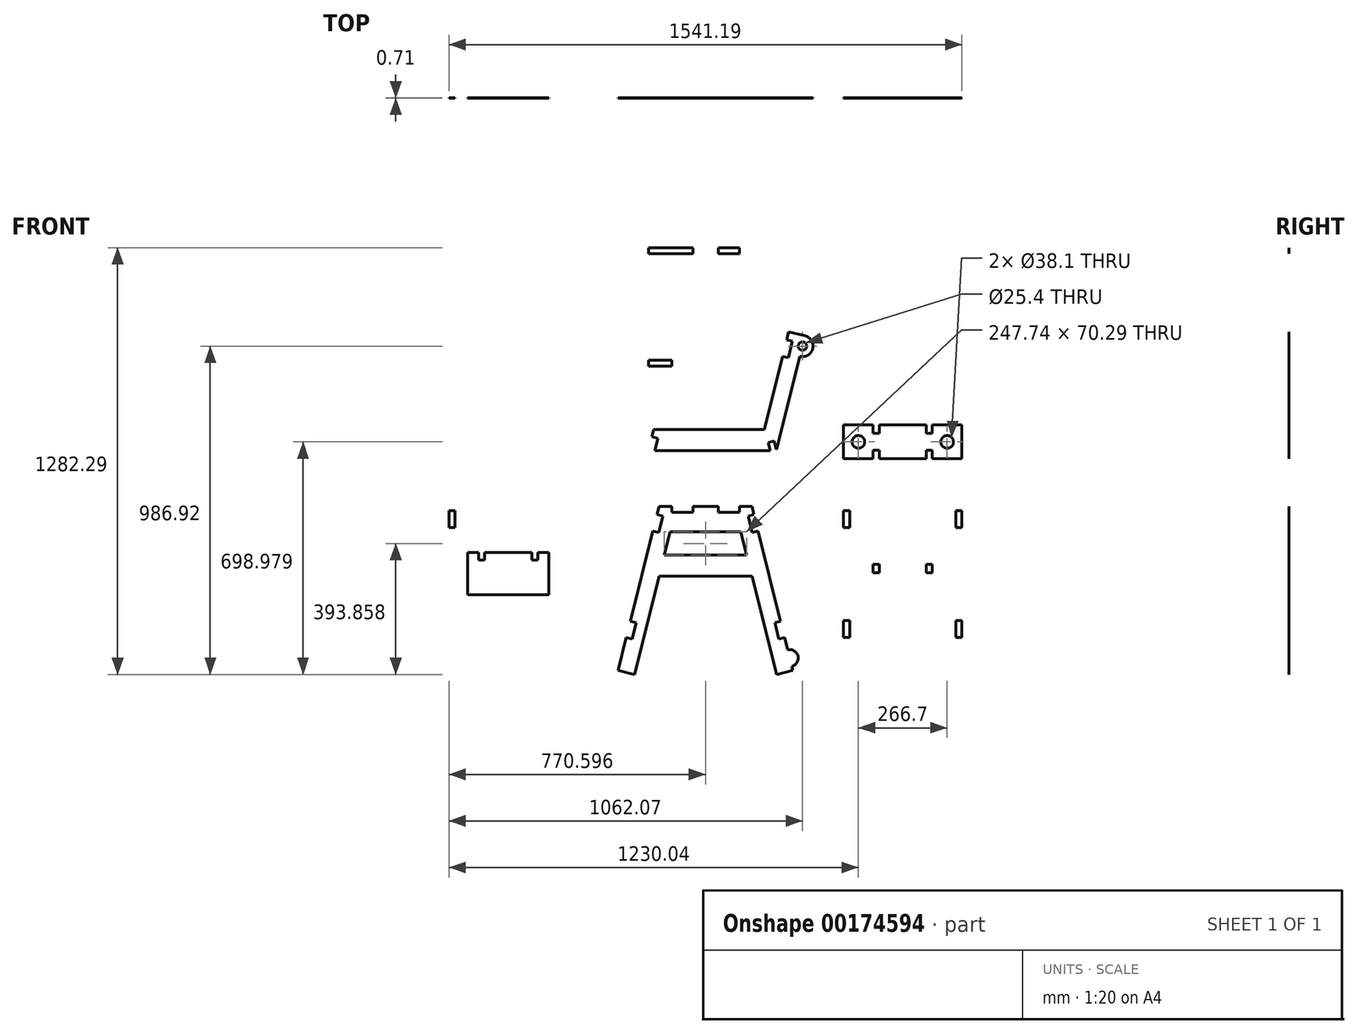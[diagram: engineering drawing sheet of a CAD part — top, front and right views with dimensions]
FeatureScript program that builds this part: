
annotation { "Feature Type Name" : "Feature", "Feature Type Description" : "" }
export const myFeature = defineFeature(function(context is Context, id is Id, definition is map)
    precondition{}
    {
        {
            assignVariable(context, id + "F0", {"name" : "MaterialThickness", "anyValue" : .71});
        }
        {
            var Q0;
            Q0=qCreatedBy(makeId("Front.planeOp"),FACE);
            var sketch = newSketch(context, id + "F1", { "sketchPlane" : qUnion([Q0])});
            skLineSegment(sketch, "E0", {"start": v(0, 0) * mm, "end": v(525.2, 0) * mm, "construction": true});
            skLineSegment(sketch, "E1", {"start": v(0, 0) * mm, "end": v(122.9, 492.91) * mm});
            skLineSegment(sketch, "E2", {"start": v(0, 0) * mm, "end": v(0, 165.04) * mm, "construction": true});
            skLineSegment(sketch, "E3", {"start": v(122.9, 492.91) * mm, "end": v(172.19, 480.62) * mm});
            skLineSegment(sketch, "E4", {"start": v(172.19, 480.62) * mm, "end": v(49.3, -12.29) * mm});
            skLineSegment(sketch, "E5", {"start": v(49.3, -12.29) * mm, "end": v(0, 0) * mm});
            skLineSegment(sketch, "E6.bottom", {"start": v(122.9, 492.91) * mm, "end": v(402.3, 492.91) * mm});
            skLineSegment(sketch, "E6.top", {"start": v(122.9, 416.71) * mm, "end": v(402.3, 416.71) * mm});
            skLineSegment(sketch, "E6.left", {"start": v(122.9, 492.91) * mm, "end": v(122.9, 416.71) * mm});
            skLineSegment(sketch, "E6.right", {"start": v(402.3, 492.91) * mm, "end": v(402.3, 416.71) * mm});
            skLineSegment(sketch, "E7", {"start": v(122.9, 282.93) * mm, "end": v(402.3, 282.93) * mm});
            skLineSegment(sketch, "E8.0", {"start": v(122.9, 346.43) * mm, "end": v(402.3, 346.43) * mm});
            skLineSegment(sketch, "E9", {"start": v(122.9, 346.43) * mm, "end": v(122.9, 282.93) * mm});
            skLineSegment(sketch, "E10", {"start": v(402.3, 282.93) * mm, "end": v(402.3, 346.43) * mm});
            skLineSegment(sketch, "E11", {"start": v(262.6, 416.71) * mm, "end": v(262.6, 0) * mm, "construction": true});
            skLineSegment(sketch, "E12.0", {"start": v(116.75, 468.26) * mm, "end": v(166.04, 455.98) * mm, "construction": true});
            skLineSegment(sketch, "E13.bottom", {"start": v(116.75, 468.26) * mm, "end": v(134.25, 463.9) * mm});
            skLineSegment(sketch, "E13.top", {"start": v(104.46, 418.97) * mm, "end": v(121.96, 414.61) * mm});
            skLineSegment(sketch, "E13.left", {"start": v(116.75, 468.26) * mm, "end": v(104.46, 418.97) * mm});
            skLineSegment(sketch, "E13.right", {"start": v(134.25, 463.9) * mm, "end": v(121.96, 414.61) * mm});
            skLineSegment(sketch, "E14.0", {"start": v(24.58, 98.58) * mm, "end": v(73.87, 86.3) * mm, "construction": true});
            skLineSegment(sketch, "E15.bottom", {"start": v(36.87, 147.87) * mm, "end": v(54.37, 143.51) * mm});
            skLineSegment(sketch, "E15.top", {"start": v(24.58, 98.58) * mm, "end": v(42.08, 94.22) * mm});
            skLineSegment(sketch, "E15.left", {"start": v(36.87, 147.87) * mm, "end": v(24.58, 98.58) * mm});
            skLineSegment(sketch, "E15.right", {"start": v(54.37, 143.51) * mm, "end": v(42.08, 94.22) * mm});
            skLineSegment(sketch, "E16.bottom", {"start": v(161, 492.91) * mm, "end": v(224.5, 492.91) * mm});
            skLineSegment(sketch, "E16.top", {"start": v(161, 474.88) * mm, "end": v(224.5, 474.88) * mm});
            skLineSegment(sketch, "E16.left", {"start": v(161, 492.91) * mm, "end": v(161, 474.88) * mm});
            skLineSegment(sketch, "E16.right", {"start": v(224.5, 492.91) * mm, "end": v(224.5, 474.88) * mm});
            skLineSegment(sketch, "E17", {"start": v(262.6, 492.91) * mm, "end": v(262.6, 416.71) * mm, "construction": true});
            skLineSegment(sketch, "E18.0", {"start": v(224.5, 492.91) * mm, "end": v(224.5, 416.71) * mm, "construction": true});
            skLineSegment(sketch, "E19.MirrorCS", {"start": v(525.2, 0) * mm, "end": v(402.3, 492.91) * mm});
            skLineSegment(sketch, "E20.MirrorCS", {"start": v(408.44, 468.26) * mm, "end": v(359.15, 455.98) * mm, "construction": true});
            skLineSegment(sketch, "E21.MirrorCS", {"start": v(500.61, 98.58) * mm, "end": v(451.32, 86.3) * mm, "construction": true});
            skLineSegment(sketch, "E22.MirrorCS", {"start": v(525.2, 0) * mm, "end": v(525.2, 165.04) * mm, "construction": true});
            skLineSegment(sketch, "E23.MirrorCS", {"start": v(353, 480.62) * mm, "end": v(475.9, -12.29) * mm});
            skLineSegment(sketch, "E24.MirrorCS", {"start": v(475.9, -12.29) * mm, "end": v(525.2, 0) * mm});
            skLineSegment(sketch, "E25.MirrorCS", {"start": v(402.3, 492.91) * mm, "end": v(353, 480.62) * mm});
            skLineSegment(sketch, "E26.MirrorCS", {"start": v(500.61, 98.58) * mm, "end": v(483.12, 94.22) * mm});
            skLineSegment(sketch, "E27.MirrorCS", {"start": v(420.73, 418.97) * mm, "end": v(403.23, 414.61) * mm});
            skLineSegment(sketch, "E28.MirrorCS", {"start": v(390.94, 463.9) * mm, "end": v(403.23, 414.61) * mm});
            skLineSegment(sketch, "E29.MirrorCS", {"start": v(488.32, 147.87) * mm, "end": v(500.61, 98.58) * mm});
            skLineSegment(sketch, "E30.MirrorCS", {"start": v(408.44, 468.26) * mm, "end": v(390.94, 463.9) * mm});
            skLineSegment(sketch, "E31.MirrorCS", {"start": v(488.32, 147.87) * mm, "end": v(470.83, 143.51) * mm});
            skLineSegment(sketch, "E32.MirrorCS", {"start": v(470.83, 143.51) * mm, "end": v(483.12, 94.22) * mm});
            skLineSegment(sketch, "E33.MirrorCS", {"start": v(408.44, 468.26) * mm, "end": v(420.73, 418.97) * mm});
            skLineSegment(sketch, "E34.MirrorCS", {"start": v(364.2, 492.91) * mm, "end": v(300.7, 492.91) * mm});
            skLineSegment(sketch, "E35.MirrorCS", {"start": v(364.2, 492.91) * mm, "end": v(364.2, 474.88) * mm});
            skLineSegment(sketch, "E36.MirrorCS", {"start": v(364.2, 474.88) * mm, "end": v(300.7, 474.88) * mm});
            skLineSegment(sketch, "E37.MirrorCS", {"start": v(300.7, 492.91) * mm, "end": v(300.7, 474.88) * mm});
            skLineSegment(sketch, "E38.bottom", {"start": v(-152.4, 98.58) * mm, "end": v(-508, 98.58) * mm});
            skLineSegment(sketch, "E38.top", {"start": v(-152.4, 479.58) * mm, "end": v(-508, 479.58) * mm});
            skLineSegment(sketch, "E38.left", {"start": v(-152.4, 98.58) * mm, "end": v(-152.4, 479.58) * mm});
            skLineSegment(sketch, "E38.right", {"start": v(-508, 98.58) * mm, "end": v(-508, 479.58) * mm});
            skLineSegment(sketch, "E39.bottom", {"start": v(-152.4, 479.58) * mm, "end": v(-170.43, 479.58) * mm});
            skLineSegment(sketch, "E39.top", {"start": v(-152.4, 428.78) * mm, "end": v(-170.43, 428.78) * mm});
            skLineSegment(sketch, "E39.left", {"start": v(-152.4, 479.58) * mm, "end": v(-152.4, 428.78) * mm});
            skLineSegment(sketch, "E39.right", {"start": v(-170.43, 479.58) * mm, "end": v(-170.43, 428.78) * mm});
            skLineSegment(sketch, "E40.bottom", {"start": v(-152.4, 98.58) * mm, "end": v(-170.43, 98.58) * mm});
            skLineSegment(sketch, "E40.top", {"start": v(-152.4, 149.38) * mm, "end": v(-170.43, 149.38) * mm});
            skLineSegment(sketch, "E40.left", {"start": v(-152.4, 98.58) * mm, "end": v(-152.4, 149.38) * mm});
            skLineSegment(sketch, "E40.right", {"start": v(-170.43, 98.58) * mm, "end": v(-170.43, 149.38) * mm});
            skLineSegment(sketch, "E41.bottom", {"start": v(-170.43, 479.58) * mm, "end": v(-208.53, 479.58) * mm});
            skLineSegment(sketch, "E41.top", {"start": v(-170.43, 98.58) * mm, "end": v(-208.53, 98.58) * mm});
            skLineSegment(sketch, "E41.left", {"start": v(-170.43, 479.58) * mm, "end": v(-170.43, 98.58) * mm});
            skLineSegment(sketch, "E41.right", {"start": v(-208.53, 479.58) * mm, "end": v(-208.53, 98.58) * mm});
            skLineSegment(sketch, "E42", {"start": v(-330.2, 479.58) * mm, "end": v(-330.2, 98.58) * mm, "construction": true});
            skLineSegment(sketch, "E43.bottom", {"start": v(-208.53, 354.01) * mm, "end": v(-330.2, 354.01) * mm});
            skLineSegment(sketch, "E43.top", {"start": v(-208.53, 227.01) * mm, "end": v(-330.2, 227.01) * mm});
            skLineSegment(sketch, "E43.left", {"start": v(-208.53, 354.01) * mm, "end": v(-208.53, 227.01) * mm});
            skLineSegment(sketch, "E43.right", {"start": v(-330.2, 354.01) * mm, "end": v(-330.2, 227.01) * mm});
            skLineSegment(sketch, "E44", {"start": v(122.9, 346.43) * mm, "end": v(86.37, 346.43) * mm, "construction": true});
            skLineSegment(sketch, "E45", {"start": v(116.75, 468.26) * mm, "end": v(86.37, 346.43) * mm, "construction": true});
            skLineSegment(sketch, "E46", {"start": v(-279.4, 354.01) * mm, "end": v(-279.4, 479.58) * mm, "construction": true});
            skLineSegment(sketch, "E47.MirrorCS", {"start": v(-489.97, 98.58) * mm, "end": v(-489.97, 149.38) * mm});
            skLineSegment(sketch, "E48.MirrorCS", {"start": v(-451.87, 354.01) * mm, "end": v(-451.87, 227.01) * mm});
            skLineSegment(sketch, "E49.MirrorCS", {"start": v(-508, 98.58) * mm, "end": v(-489.97, 98.58) * mm});
            skLineSegment(sketch, "E50.MirrorCS", {"start": v(-489.97, 479.58) * mm, "end": v(-489.97, 428.78) * mm});
            skLineSegment(sketch, "E51.MirrorCS", {"start": v(-508, 149.38) * mm, "end": v(-489.97, 149.38) * mm});
            skLineSegment(sketch, "E52.MirrorCS", {"start": v(-451.87, 354.01) * mm, "end": v(-330.2, 354.01) * mm});
            skLineSegment(sketch, "E53.MirrorCS", {"start": v(-451.87, 227.01) * mm, "end": v(-330.2, 227.01) * mm});
            skLineSegment(sketch, "E54.MirrorCS", {"start": v(-508, 428.78) * mm, "end": v(-489.97, 428.78) * mm});
            skLineSegment(sketch, "E55.MirrorCS", {"start": v(-508, 98.58) * mm, "end": v(-508, 149.38) * mm});
            skLineSegment(sketch, "E56.MirrorCS", {"start": v(-489.97, 479.58) * mm, "end": v(-451.87, 479.58) * mm});
            skLineSegment(sketch, "E57.MirrorCS", {"start": v(-489.97, 479.58) * mm, "end": v(-489.97, 98.58) * mm});
            skLineSegment(sketch, "E58.MirrorCS", {"start": v(-489.97, 98.58) * mm, "end": v(-451.87, 98.58) * mm});
            skLineSegment(sketch, "E59.MirrorCS", {"start": v(-508, 479.58) * mm, "end": v(-489.97, 479.58) * mm});
            skLineSegment(sketch, "E60.MirrorCS", {"start": v(-451.87, 479.58) * mm, "end": v(-451.87, 98.58) * mm});
            skLineSegment(sketch, "E61.MirrorCS", {"start": v(-508, 479.58) * mm, "end": v(-508, 428.78) * mm});
            skLineSegment(sketch, "E62", {"start": v(121.96, 414.61) * mm, "end": v(54.37, 143.51) * mm, "construction": true});
            skLineSegment(sketch, "E63.bottom", {"start": v(405.36, 295.21) * mm, "end": v(454.65, 282.93) * mm, "construction": true});
            skLineSegment(sketch, "E63.top", {"start": v(491.39, 640.25) * mm, "end": v(540.68, 627.96) * mm, "construction": true});
            skLineSegment(sketch, "E63.left", {"start": v(405.36, 295.21) * mm, "end": v(491.39, 640.25) * mm, "construction": true});
            skLineSegment(sketch, "E63.right", {"start": v(454.65, 282.93) * mm, "end": v(540.68, 627.96) * mm, "construction": true});
            skLineSegment(sketch, "E64", {"start": v(402.3, 282.93) * mm, "end": v(454.65, 282.93) * mm, "construction": true});
            skLineSegment(sketch, "E65", {"start": v(470.83, 143.51) * mm, "end": v(403.23, 414.61) * mm, "construction": true});
            skLineSegment(sketch, "E66", {"start": v(436.07, 282.93) * mm, "end": v(453.56, 287.29) * mm, "construction": true});
            skLineSegment(sketch, "E67", {"start": v(453.56, 287.29) * mm, "end": v(473.5, 292.26) * mm, "construction": true});
            skLineSegment(sketch, "E68.0", {"start": v(429.92, 307.57) * mm, "end": v(447.42, 311.93) * mm, "construction": true});
            skLineSegment(sketch, "E69", {"start": v(402.3, 346.43) * mm, "end": v(418.13, 346.43) * mm, "construction": true});
            skLineSegment(sketch, "E70", {"start": v(427.76, 390.8) * mm, "end": v(410.26, 386.44) * mm});
            skLineSegment(sketch, "E71", {"start": v(122.9, 282.93) * mm, "end": v(70.54, 282.93) * mm, "construction": true});
            skLineSegment(sketch, "E72", {"start": v(89.13, 282.93) * mm, "end": v(71.63, 287.29) * mm, "construction": true});
            skLineSegment(sketch, "E73.bottom", {"start": v(71.63, 287.29) * mm, "end": v(89.13, 282.93) * mm, "construction": true});
            skLineSegment(sketch, "E73.top", {"start": v(80.85, 324.26) * mm, "end": v(98.34, 319.9) * mm, "construction": true});
            skLineSegment(sketch, "E73.left", {"start": v(71.63, 287.29) * mm, "end": v(80.85, 324.26) * mm, "construction": true});
            skLineSegment(sketch, "E73.right", {"start": v(89.13, 282.93) * mm, "end": v(98.34, 319.9) * mm, "construction": true});
            skLineSegment(sketch, "E74.bottom", {"start": v(677.6, 98.58) * mm, "end": v(1033.2, 98.58) * mm});
            skLineSegment(sketch, "E74.top", {"start": v(677.6, 479.58) * mm, "end": v(1033.2, 479.58) * mm});
            skLineSegment(sketch, "E74.left", {"start": v(677.6, 98.58) * mm, "end": v(677.6, 479.58) * mm});
            skLineSegment(sketch, "E74.right", {"start": v(1033.2, 98.58) * mm, "end": v(1033.2, 479.58) * mm});
            skLineSegment(sketch, "E75", {"start": v(855.4, 479.58) * mm, "end": v(855.4, 98.58) * mm, "construction": true});
            skLineSegment(sketch, "E76.bottom", {"start": v(677.6, 479.58) * mm, "end": v(695.63, 479.58) * mm});
            skLineSegment(sketch, "E76.top", {"start": v(677.6, 428.78) * mm, "end": v(695.63, 428.78) * mm});
            skLineSegment(sketch, "E76.left", {"start": v(677.6, 479.58) * mm, "end": v(677.6, 428.78) * mm});
            skLineSegment(sketch, "E76.right", {"start": v(695.63, 479.58) * mm, "end": v(695.63, 428.78) * mm});
            skLineSegment(sketch, "E77.bottom", {"start": v(695.63, 149.38) * mm, "end": v(677.6, 149.38) * mm});
            skLineSegment(sketch, "E77.top", {"start": v(695.63, 98.58) * mm, "end": v(677.6, 98.58) * mm});
            skLineSegment(sketch, "E77.left", {"start": v(695.63, 149.38) * mm, "end": v(695.63, 98.58) * mm});
            skLineSegment(sketch, "E77.right", {"start": v(677.6, 149.38) * mm, "end": v(677.6, 98.58) * mm});
            skLineSegment(sketch, "E78.bottom", {"start": v(695.63, 479.58) * mm, "end": v(733.73, 479.58) * mm});
            skLineSegment(sketch, "E78.top", {"start": v(695.63, 98.58) * mm, "end": v(733.73, 98.58) * mm});
            skLineSegment(sketch, "E78.left", {"start": v(695.63, 479.58) * mm, "end": v(695.63, 98.58) * mm});
            skLineSegment(sketch, "E78.right", {"start": v(733.73, 479.58) * mm, "end": v(733.73, 98.58) * mm});
            skPoint(sketch, "E79", {"position": v(419, 388.62) * mm});
            skLineSegment(sketch, "E80", {"start": v(419, 388.62) * mm, "end": v(399.7, 466.08) * mm, "construction": true});
            skLineSegment(sketch, "E81.bottom", {"start": v(-330.2, 354.01) * mm, "end": v(-241.3, 354.01) * mm, "construction": true});
            skLineSegment(sketch, "E81.top", {"start": v(-330.2, 331.16) * mm, "end": v(-241.3, 331.16) * mm, "construction": true});
            skLineSegment(sketch, "E81.left", {"start": v(-330.2, 354.01) * mm, "end": v(-330.2, 331.16) * mm, "construction": true});
            skLineSegment(sketch, "E81.right", {"start": v(-241.3, 354.01) * mm, "end": v(-241.3, 331.16) * mm, "construction": true});
            skLineSegment(sketch, "E82", {"start": v(86.37, 346.43) * mm, "end": v(80.85, 324.26) * mm, "construction": true});
            skLineSegment(sketch, "E83.bottom", {"start": v(-241.3, 354.01) * mm, "end": v(-259.33, 354.01) * mm});
            skLineSegment(sketch, "E83.top", {"start": v(-241.3, 331.16) * mm, "end": v(-259.33, 331.16) * mm});
            skLineSegment(sketch, "E83.left", {"start": v(-241.3, 354.01) * mm, "end": v(-241.3, 331.16) * mm});
            skLineSegment(sketch, "E83.right", {"start": v(-259.33, 354.01) * mm, "end": v(-259.33, 331.16) * mm});
            skLineSegment(sketch, "E84.MirrorCS", {"start": v(-419.1, 354.01) * mm, "end": v(-419.1, 331.16) * mm});
            skLineSegment(sketch, "E85.MirrorCS", {"start": v(-401.07, 354.01) * mm, "end": v(-401.07, 331.16) * mm});
            skLineSegment(sketch, "E86.MirrorCS", {"start": v(-419.1, 354.01) * mm, "end": v(-419.1, 331.16) * mm, "construction": true});
            skLineSegment(sketch, "E87.MirrorCS", {"start": v(-419.1, 354.01) * mm, "end": v(-401.07, 354.01) * mm});
            skLineSegment(sketch, "E88.MirrorCS", {"start": v(-419.1, 331.16) * mm, "end": v(-401.07, 331.16) * mm});
            skLineSegment(sketch, "E89.bottom", {"start": v(855.4, 399.74) * mm, "end": v(766.5, 399.74) * mm, "construction": true});
            skLineSegment(sketch, "E89.top", {"start": v(855.4, 318.46) * mm, "end": v(766.5, 318.46) * mm, "construction": true});
            skLineSegment(sketch, "E89.left", {"start": v(855.4, 399.74) * mm, "end": v(855.4, 318.46) * mm, "construction": true});
            skLineSegment(sketch, "E89.right", {"start": v(766.5, 399.74) * mm, "end": v(766.5, 318.46) * mm, "construction": true});
            skLineSegment(sketch, "E90", {"start": v(810.94, 399.74) * mm, "end": v(810.94, 479.58) * mm, "construction": true});
            skLineSegment(sketch, "E91.bottom", {"start": v(766.5, 399.74) * mm, "end": v(784.53, 399.74) * mm});
            skLineSegment(sketch, "E91.top", {"start": v(766.5, 318.46) * mm, "end": v(784.53, 318.46) * mm});
            skLineSegment(sketch, "E91.left", {"start": v(766.5, 399.74) * mm, "end": v(766.5, 318.46) * mm});
            skLineSegment(sketch, "E91.right", {"start": v(784.53, 399.74) * mm, "end": v(784.53, 318.46) * mm});
            skLineSegment(sketch, "E92.top", {"start": v(766.5, 293.06) * mm, "end": v(784.53, 293.06) * mm});
            skLineSegment(sketch, "E92.left", {"start": v(766.5, 318.46) * mm, "end": v(766.5, 293.06) * mm});
            skLineSegment(sketch, "E92.right", {"start": v(784.53, 318.46) * mm, "end": v(784.53, 293.06) * mm});
            skLineSegment(sketch, "E93.bottom", {"start": v(733.73, 98.58) * mm, "end": v(855.4, 98.58) * mm});
            skLineSegment(sketch, "E93.top", {"start": v(733.73, 191.46) * mm, "end": v(855.4, 191.46) * mm});
            skLineSegment(sketch, "E93.left", {"start": v(733.73, 98.58) * mm, "end": v(733.73, 191.46) * mm});
            skLineSegment(sketch, "E93.right", {"start": v(855.4, 98.58) * mm, "end": v(855.4, 191.46) * mm});
            skLineSegment(sketch, "E94.bottom", {"start": v(765.86, 191.46) * mm, "end": v(785.16, 191.46) * mm});
            skLineSegment(sketch, "E94.top", {"start": v(765.86, 293.06) * mm, "end": v(785.16, 293.06) * mm});
            skLineSegment(sketch, "E94.left", {"start": v(765.86, 191.46) * mm, "end": v(765.86, 293.06) * mm});
            skLineSegment(sketch, "E94.right", {"start": v(785.16, 191.46) * mm, "end": v(785.16, 293.06) * mm});
            skPoint(sketch, "E95", {"position": v(775.5, 293.06) * mm});
            skLineSegment(sketch, "E96.MirrorCS", {"start": v(977.06, 98.58) * mm, "end": v(855.4, 98.58) * mm});
            skLineSegment(sketch, "E97.MirrorCS", {"start": v(977.06, 191.46) * mm, "end": v(855.4, 191.46) * mm});
            skLineSegment(sketch, "E98.MirrorCS", {"start": v(855.4, 399.74) * mm, "end": v(944.3, 399.74) * mm, "construction": true});
            skLineSegment(sketch, "E99.MirrorCS", {"start": v(944.3, 399.74) * mm, "end": v(944.3, 318.46) * mm, "construction": true});
            skLineSegment(sketch, "E100.MirrorCS", {"start": v(855.4, 318.46) * mm, "end": v(944.3, 318.46) * mm, "construction": true});
            skLineSegment(sketch, "E101.MirrorCS", {"start": v(944.3, 293.06) * mm, "end": v(926.26, 293.06) * mm});
            skLineSegment(sketch, "E102.MirrorCS", {"start": v(944.93, 293.06) * mm, "end": v(925.62, 293.06) * mm});
            skPoint(sketch, "E103.MirrorP", {"position": v(935.28, 293.06) * mm});
            skLineSegment(sketch, "E104.MirrorCS", {"start": v(1015.16, 479.58) * mm, "end": v(1015.16, 428.78) * mm});
            skLineSegment(sketch, "E105.MirrorCS", {"start": v(1033.2, 149.38) * mm, "end": v(1033.2, 98.58) * mm});
            skLineSegment(sketch, "E106.MirrorCS", {"start": v(1033.2, 479.58) * mm, "end": v(1033.2, 428.78) * mm});
            skLineSegment(sketch, "E107.MirrorCS", {"start": v(944.3, 318.46) * mm, "end": v(926.26, 318.46) * mm});
            skLineSegment(sketch, "E108.MirrorCS", {"start": v(944.3, 399.74) * mm, "end": v(944.3, 318.46) * mm});
            skLineSegment(sketch, "E109.MirrorCS", {"start": v(1015.16, 149.38) * mm, "end": v(1015.16, 98.58) * mm});
            skLineSegment(sketch, "E110.MirrorCS", {"start": v(926.26, 399.74) * mm, "end": v(926.26, 318.46) * mm});
            skLineSegment(sketch, "E111.MirrorCS", {"start": v(1015.16, 149.38) * mm, "end": v(1033.2, 149.38) * mm});
            skLineSegment(sketch, "E112.MirrorCS", {"start": v(926.26, 318.46) * mm, "end": v(926.26, 293.06) * mm});
            skLineSegment(sketch, "E113.MirrorCS", {"start": v(1015.16, 98.58) * mm, "end": v(977.06, 98.58) * mm});
            skLineSegment(sketch, "E114.MirrorCS", {"start": v(1015.16, 98.58) * mm, "end": v(1033.2, 98.58) * mm});
            skLineSegment(sketch, "E115.MirrorCS", {"start": v(977.06, 479.58) * mm, "end": v(977.06, 98.58) * mm});
            skLineSegment(sketch, "E116.MirrorCS", {"start": v(944.3, 318.46) * mm, "end": v(944.3, 293.06) * mm});
            skLineSegment(sketch, "E117.MirrorCS", {"start": v(1015.16, 479.58) * mm, "end": v(977.06, 479.58) * mm});
            skLineSegment(sketch, "E118.MirrorCS", {"start": v(925.62, 191.46) * mm, "end": v(925.62, 293.06) * mm});
            skLineSegment(sketch, "E119.MirrorCS", {"start": v(1033.2, 479.58) * mm, "end": v(1015.16, 479.58) * mm});
            skLineSegment(sketch, "E120.MirrorCS", {"start": v(944.3, 399.74) * mm, "end": v(926.26, 399.74) * mm});
            skLineSegment(sketch, "E121.MirrorCS", {"start": v(977.06, 98.58) * mm, "end": v(977.06, 191.46) * mm});
            skLineSegment(sketch, "E122.MirrorCS", {"start": v(1015.16, 479.58) * mm, "end": v(1015.16, 98.58) * mm});
            skLineSegment(sketch, "E123.MirrorCS", {"start": v(1033.2, 428.78) * mm, "end": v(1015.16, 428.78) * mm});
            skLineSegment(sketch, "E124.MirrorCS", {"start": v(944.93, 191.46) * mm, "end": v(925.62, 191.46) * mm});
            skLineSegment(sketch, "E125.MirrorCS", {"start": v(944.93, 191.46) * mm, "end": v(944.93, 293.06) * mm});
            skLineSegment(sketch, "E126.bottom", {"start": v(491.39, 640.25) * mm, "end": v(508.89, 635.89) * mm, "construction": true});
            skLineSegment(sketch, "E126.top", {"start": v(472.95, 566.32) * mm, "end": v(490.45, 561.95) * mm, "construction": true});
            skLineSegment(sketch, "E126.left", {"start": v(491.39, 640.25) * mm, "end": v(472.95, 566.32) * mm, "construction": true});
            skLineSegment(sketch, "E126.right", {"start": v(508.89, 635.89) * mm, "end": v(490.45, 561.95) * mm, "construction": true});
            skLineSegment(sketch, "E127.bottom", {"start": v(485.24, 615.6) * mm, "end": v(502.74, 611.24) * mm, "construction": true});
            skLineSegment(sketch, "E127.left", {"start": v(485.24, 615.6) * mm, "end": v(491.39, 640.25) * mm, "construction": true});
            skLineSegment(sketch, "E127.right", {"start": v(502.74, 611.24) * mm, "end": v(508.89, 635.89) * mm, "construction": true});
            skLineSegment(sketch, "E128.bottom", {"start": v(677.6, 635.89) * mm, "end": v(1033.2, 635.89) * mm});
            skLineSegment(sketch, "E128.top", {"start": v(677.6, 737.49) * mm, "end": v(1033.2, 737.49) * mm});
            skLineSegment(sketch, "E128.left", {"start": v(677.6, 635.89) * mm, "end": v(677.6, 737.49) * mm});
            skLineSegment(sketch, "E128.right", {"start": v(1033.2, 635.89) * mm, "end": v(1033.2, 737.49) * mm});
            skLineSegment(sketch, "E129.bottom", {"start": v(766.5, 635.89) * mm, "end": v(784.53, 635.89) * mm});
            skLineSegment(sketch, "E129.top", {"start": v(766.5, 661.29) * mm, "end": v(784.53, 661.29) * mm});
            skLineSegment(sketch, "E129.left", {"start": v(766.5, 635.89) * mm, "end": v(766.5, 661.29) * mm});
            skLineSegment(sketch, "E129.right", {"start": v(784.53, 635.89) * mm, "end": v(784.53, 661.29) * mm});
            skLineSegment(sketch, "E130", {"start": v(855.4, 737.49) * mm, "end": v(855.4, 635.89) * mm, "construction": true});
            skLineSegment(sketch, "E131.MirrorCS", {"start": v(926.26, 635.89) * mm, "end": v(926.26, 661.29) * mm});
            skLineSegment(sketch, "E132.MirrorCS", {"start": v(944.3, 635.89) * mm, "end": v(926.26, 635.89) * mm});
            skLineSegment(sketch, "E133.MirrorCS", {"start": v(944.3, 661.29) * mm, "end": v(926.26, 661.29) * mm});
            skLineSegment(sketch, "E134.MirrorCS", {"start": v(944.3, 635.89) * mm, "end": v(944.3, 661.29) * mm});
            skLineSegment(sketch, "E135", {"start": v(677.6, 686.69) * mm, "end": v(1033.2, 686.69) * mm, "construction": true});
            skLineSegment(sketch, "E136.MirrorCS", {"start": v(926.26, 737.49) * mm, "end": v(926.26, 712.09) * mm});
            skLineSegment(sketch, "E137.MirrorCS", {"start": v(944.3, 737.49) * mm, "end": v(926.26, 737.49) * mm});
            skLineSegment(sketch, "E138.MirrorCS", {"start": v(944.3, 712.09) * mm, "end": v(926.26, 712.09) * mm});
            skLineSegment(sketch, "E139.MirrorCS", {"start": v(944.3, 737.49) * mm, "end": v(944.3, 712.09) * mm});
            skLineSegment(sketch, "E140.MirrorCS", {"start": v(784.53, 737.49) * mm, "end": v(784.53, 712.09) * mm});
            skLineSegment(sketch, "E141.MirrorCS", {"start": v(766.5, 737.49) * mm, "end": v(784.53, 737.49) * mm});
            skLineSegment(sketch, "E142.MirrorCS", {"start": v(766.5, 737.49) * mm, "end": v(766.5, 712.09) * mm});
            skLineSegment(sketch, "E143.MirrorCS", {"start": v(766.5, 712.09) * mm, "end": v(784.53, 712.09) * mm});
            skLineSegment(sketch, "E144", {"start": v(766.5, 712.09) * mm, "end": v(766.5, 661.29) * mm, "construction": true});
            skLineSegment(sketch, "E145", {"start": v(766.5, 686.69) * mm, "end": v(677.6, 686.69) * mm, "construction": true});
            skCircle(sketch, "E146", {"center": v(722.04, 686.69) * mm, "radius": 19.05 * mm});
            skCircle(sketch, "E147.MirrorC", {"center": v(988.74, 686.69) * mm, "radius": 19.05 * mm});
            skPoint(sketch, "E148", {"position": v(533, 597.16) * mm});
            skPoint(sketch, "E149", {"position": v(515.98, 36.97) * mm});
            skCircle(sketch, "E150", {"center": v(515.98, 36.97) * mm, "radius": 25.4 * mm});
            skCircle(sketch, "E151", {"center": v(515.98, 36.97) * mm, "radius": 38.1 * mm});
            skLineSegment(sketch, "E152", {"start": v(143.97, 660.4) * mm, "end": v(423.37, 660.4) * mm});
            skLineSegment(sketch, "E153.0", {"start": v(143.97, 723.9) * mm, "end": v(423.37, 723.9) * mm});
            skLineSegment(sketch, "E154", {"start": v(143.97, 723.9) * mm, "end": v(143.97, 660.4) * mm});
            skLineSegment(sketch, "E155", {"start": v(143.97, 723.9) * mm, "end": v(107.44, 723.9) * mm});
            skLineSegment(sketch, "E156.top", {"start": v(512.46, 1017.73) * mm, "end": v(561.75, 1005.44) * mm});
            skLineSegment(sketch, "E156.left", {"start": v(439.2, 723.9) * mm, "end": v(512.46, 1017.73) * mm});
            skLineSegment(sketch, "E156.right", {"start": v(476.95, 665.34) * mm, "end": v(561.75, 1005.44) * mm});
            skLineSegment(sketch, "E157.0", {"start": v(450.99, 685.05) * mm, "end": v(468.49, 689.4) * mm});
            skLineSegment(sketch, "E158", {"start": v(423.37, 723.9) * mm, "end": v(439.2, 723.9) * mm});
            skLineSegment(sketch, "E159", {"start": v(110.2, 660.4) * mm, "end": v(92.7, 664.76) * mm, "construction": true});
            skLineSegment(sketch, "E160.bottom", {"start": v(92.7, 664.76) * mm, "end": v(110.2, 660.4) * mm, "construction": true});
            skLineSegment(sketch, "E160.top", {"start": v(101.92, 701.73) * mm, "end": v(119.41, 697.37) * mm});
            skLineSegment(sketch, "E160.left", {"start": v(92.7, 664.76) * mm, "end": v(101.92, 701.73) * mm, "construction": true});
            skLineSegment(sketch, "E160.right", {"start": v(110.2, 660.4) * mm, "end": v(119.41, 697.37) * mm});
            skLineSegment(sketch, "E161", {"start": v(107.44, 723.9) * mm, "end": v(101.92, 701.73) * mm});
            skLineSegment(sketch, "E162.bottom", {"start": v(512.46, 1017.73) * mm, "end": v(529.96, 1013.36) * mm, "construction": true});
            skLineSegment(sketch, "E162.top", {"start": v(494.02, 943.8) * mm, "end": v(511.52, 939.43) * mm});
            skLineSegment(sketch, "E162.left", {"start": v(512.46, 1017.73) * mm, "end": v(494.02, 943.8) * mm});
            skLineSegment(sketch, "E162.right", {"start": v(529.96, 1013.36) * mm, "end": v(511.52, 939.43) * mm});
            skLineSegment(sketch, "E163.bottom", {"start": v(506.31, 993.08) * mm, "end": v(523.81, 988.72) * mm});
            skLineSegment(sketch, "E163.left", {"start": v(506.31, 993.08) * mm, "end": v(512.46, 1017.73) * mm, "construction": true});
            skLineSegment(sketch, "E163.right", {"start": v(523.81, 988.72) * mm, "end": v(529.96, 1013.36) * mm, "construction": true});
            skPoint(sketch, "E164", {"position": v(554.07, 974.63) * mm});
            skLineSegment(sketch, "E165", {"start": v(143.97, 660.4) * mm, "end": v(110.2, 660.4) * mm});
            skPoint(sketch, "E166", {"position": v(476.95, 665.34) * mm});
            skLineSegment(sketch, "E167", {"start": v(457.13, 660.4) * mm, "end": v(450.99, 685.05) * mm});
            skLineSegment(sketch, "E168", {"start": v(468.49, 689.4) * mm, "end": v(474.63, 664.76) * mm});
            skLineSegment(sketch, "E169", {"start": v(474.63, 664.76) * mm, "end": v(476.95, 665.34) * mm});
            skLineSegment(sketch, "E170", {"start": v(457.13, 660.4) * mm, "end": v(423.37, 660.4) * mm});
            skCircle(sketch, "E171", {"center": v(554.07, 974.63) * mm, "radius": 31.75 * mm});
            skCircle(sketch, "E172", {"center": v(554.07, 974.63) * mm, "radius": 12.7 * mm});
            skPoint(sketch, "E173", {"position": v(439.2, 723.9) * mm});
            skPoint(sketch, "E174", {"position": v(262.6, 492.91) * mm});
            skLineSegment(sketch, "E175.bottom", {"start": v(91.15, 914.4) * mm, "end": v(434.05, 914.4) * mm});
            skLineSegment(sketch, "E175.top", {"start": v(91.15, 1270) * mm, "end": v(434.05, 1270) * mm});
            skLineSegment(sketch, "E175.left", {"start": v(91.15, 914.4) * mm, "end": v(91.15, 1270) * mm});
            skLineSegment(sketch, "E175.right", {"start": v(434.05, 914.4) * mm, "end": v(434.05, 1270) * mm});
            skPoint(sketch, "E176", {"position": v(262.6, 914.4) * mm});
            skLineSegment(sketch, "E177.top", {"start": v(91.15, 932.43) * mm, "end": v(434.05, 932.43) * mm});
            skLineSegment(sketch, "E177.left", {"start": v(91.15, 914.4) * mm, "end": v(91.15, 932.43) * mm});
            skLineSegment(sketch, "E177.right", {"start": v(434.05, 914.4) * mm, "end": v(434.05, 932.43) * mm});
            skLineSegment(sketch, "E178.bottom", {"start": v(224.5, 914.4) * mm, "end": v(161, 914.4) * mm});
            skLineSegment(sketch, "E178.top", {"start": v(224.5, 932.43) * mm, "end": v(161, 932.43) * mm});
            skLineSegment(sketch, "E178.left", {"start": v(224.5, 914.4) * mm, "end": v(224.5, 932.43) * mm});
            skLineSegment(sketch, "E178.right", {"start": v(161, 914.4) * mm, "end": v(161, 932.43) * mm});
            skLineSegment(sketch, "E179.bottom", {"start": v(300.7, 914.4) * mm, "end": v(364.2, 914.4) * mm});
            skLineSegment(sketch, "E179.top", {"start": v(300.7, 932.43) * mm, "end": v(364.2, 932.43) * mm});
            skLineSegment(sketch, "E179.left", {"start": v(300.7, 914.4) * mm, "end": v(300.7, 932.43) * mm});
            skLineSegment(sketch, "E179.right", {"start": v(364.2, 914.4) * mm, "end": v(364.2, 932.43) * mm});
            skLineSegment(sketch, "E180", {"start": v(91.15, 1092.2) * mm, "end": v(434.05, 1092.2) * mm, "construction": true});
            skLineSegment(sketch, "E181.MirrorCS", {"start": v(364.2, 1270) * mm, "end": v(364.2, 1251.97) * mm});
            skLineSegment(sketch, "E182.MirrorCS", {"start": v(434.05, 1270) * mm, "end": v(434.05, 1251.97) * mm});
            skLineSegment(sketch, "E183.MirrorCS", {"start": v(224.5, 1270) * mm, "end": v(224.5, 1251.97) * mm});
            skLineSegment(sketch, "E184.MirrorCS", {"start": v(91.15, 1270) * mm, "end": v(91.15, 1251.97) * mm});
            skLineSegment(sketch, "E185.MirrorCS", {"start": v(161, 1270) * mm, "end": v(161, 1251.97) * mm});
            skLineSegment(sketch, "E186.MirrorCS", {"start": v(300.7, 1270) * mm, "end": v(300.7, 1251.97) * mm});
            skLineSegment(sketch, "E187.MirrorCS", {"start": v(224.5, 1270) * mm, "end": v(161, 1270) * mm});
            skLineSegment(sketch, "E188.MirrorCS", {"start": v(300.7, 1270) * mm, "end": v(364.2, 1270) * mm});
            skLineSegment(sketch, "E189.MirrorCS", {"start": v(300.7, 1251.97) * mm, "end": v(364.2, 1251.97) * mm});
            skLineSegment(sketch, "E190.MirrorCS", {"start": v(91.15, 1251.97) * mm, "end": v(434.05, 1251.97) * mm});
            skLineSegment(sketch, "E191.MirrorCS", {"start": v(224.5, 1251.97) * mm, "end": v(161, 1251.97) * mm});
            skPoint(sketch, "E192.MirrorP", {"position": v(262.6, 1270) * mm});
            skLineSegment(sketch, "E193", {"start": v(192.75, 1251.97) * mm, "end": v(192.75, 932.43) * mm, "construction": true});
            skLineSegment(sketch, "E194", {"start": v(332.45, 1251.97) * mm, "end": v(332.45, 932.43) * mm, "construction": true});
            skLineSegment(sketch, "E195.bottom", {"start": v(205.45, 1143) * mm, "end": v(180.05, 1143) * mm});
            skLineSegment(sketch, "E195.top", {"start": v(205.45, 1041.4) * mm, "end": v(180.05, 1041.4) * mm});
            skLineSegment(sketch, "E195.left", {"start": v(205.45, 1143) * mm, "end": v(205.45, 1041.4) * mm});
            skLineSegment(sketch, "E195.right", {"start": v(180.05, 1143) * mm, "end": v(180.05, 1041.4) * mm});
            skPoint(sketch, "E195.middle", {"position": v(192.75, 1092.2) * mm});
            skLineSegment(sketch, "E196.bottom", {"start": v(345.15, 1143) * mm, "end": v(319.75, 1143) * mm});
            skLineSegment(sketch, "E196.top", {"start": v(345.15, 1041.4) * mm, "end": v(319.75, 1041.4) * mm});
            skLineSegment(sketch, "E196.left", {"start": v(345.15, 1143) * mm, "end": v(345.15, 1041.4) * mm});
            skLineSegment(sketch, "E196.right", {"start": v(319.75, 1143) * mm, "end": v(319.75, 1041.4) * mm});
            skPoint(sketch, "E196.middle", {"position": v(332.45, 1092.2) * mm});
            skSolve(sketch);
        }
        {
            var Q0;
            {var subQ3=sQuery(id+"F1.wireOp",EDGE,"E175.left");Q0=makeQuery(id+"F1.imprint","IMPRINT",FACE,{"disambiguationData":[TD([[makeQuery(id+"F1.imprint","IMPRINT",EDGE,{"derivedFrom":subQ3}),-1.0]])]});}
            var Q1;
            {var subQ0=sQuery(id+"F1.wireOp",EDGE,"E181.MirrorCS");Q1=makeQuery(id+"F1.imprint","IMPRINT",FACE,{"disambiguationData":[TD([[makeQuery(id+"F1.imprint","IMPRINT",EDGE,{"derivedFrom":subQ0}),-1.0]])]});}
            var Q2;
            {var subQ0=sQuery(id+"F1.wireOp",EDGE,"E183.MirrorCS");Q2=makeQuery(id+"F1.imprint","IMPRINT",FACE,{"disambiguationData":[TD([[makeQuery(id+"F1.imprint","IMPRINT",EDGE,{"derivedFrom":subQ0}),-1.0]])]});}
            var Q3;
            Q3=makeQuery(id+"F1.imprint","IMPRINT",FACE,{"disambiguationData":[TD([[makeQuery(id+"F1.imprint","IMPRINT",EDGE,{"derivedFrom":sQuery(id+"F1.wireOp",EDGE,"E178.bottom")}),-1.0]])]});
            var Q4;
            Q4=makeQuery(id+"F1.imprint","IMPRINT",FACE,{"disambiguationData":[TD([[makeQuery(id+"F1.imprint","IMPRINT",EDGE,{"derivedFrom":sQuery(id+"F1.wireOp",EDGE,"E179.bottom")}),1.0]])]});
            extrude(context, id + "F2", {"entities" : qUnion([Q0, Q1, Q2, Q3, Q4]), "depth" : (getVariable(context, 'MaterialThickness')) * mm});
        }
        {
            var Q0;
            Q0=makeQuery(id+"F1.imprint","IMPRINT",FACE,{"disambiguationData":[TD([[makeQuery(id+"F1.imprint","IMPRINT",EDGE,{"derivedFrom":sQuery(id+"F1.wireOp",EDGE,"E152")}),1.0]])]});
            var Q1;
            Q1=makeQuery(id+"F1.imprint","IMPRINT",FACE,{"disambiguationData":[TD([[makeQuery(id+"F1.imprint","IMPRINT",EDGE,{"derivedFrom":sQuery(id+"F1.wireOp",EDGE,"E154")}),-1.0]])]});
            var Q2;
            {var subQ5=sQuery(id+"F1.wireOp",EDGE,"E163.bottom");Q2=makeQuery(id+"F1.imprint","IMPRINT",FACE,{"disambiguationData":[TD([[makeQuery(id+"F1.imprint","IMPRINT",EDGE,{"derivedFrom":subQ5}),1.0]])]});}
            var Q3;
            {var subQ0=sQuery(id+"F1.wireOp",EDGE,"E171");var subQ1=sQuery(id+"F1.wireOp",EDGE,"E156.right");var subQ2=makeQuery(id+"F1.imprint","INTERSECT",VERTEX,{"derivedFrom":[subQ1,subQ0]});Q3=makeQuery(id+"F1.imprint","IMPRINT",FACE,{"disambiguationData":[TD([[makeQuery(id+"F1.imprint","IMPRINT",EDGE,{"disambiguationData":[TD([[subQ2,-1.0]])],"derivedFrom":subQ1}),1.0]])]});}
            var Q4;
            {var subQ0=sQuery(id+"F1.wireOp",EDGE,"E171");var subQ1=sQuery(id+"F1.wireOp",EDGE,"E156.right");var subQ2=makeQuery(id+"F1.imprint","INTERSECT",VERTEX,{"derivedFrom":[subQ1,subQ0]});Q4=makeQuery(id+"F1.imprint","IMPRINT",FACE,{"disambiguationData":[TD([[makeQuery(id+"F1.imprint","IMPRINT",EDGE,{"disambiguationData":[TD([[subQ2,-1.0]])],"derivedFrom":subQ1}),-1.0]])]});}
            extrude(context, id + "F3", {"entities" : qUnion([Q0, Q1, Q2, Q3, Q4]), "depth" : (getVariable(context, 'MaterialThickness')) * mm});
        }
        {
            var Q0;
            {var subQ0=sQuery(id+"F1.wireOp",EDGE,"E128.left");Q0=makeQuery(id+"F1.imprint","IMPRINT",FACE,{"disambiguationData":[TD([[makeQuery(id+"F1.imprint","IMPRINT",EDGE,{"derivedFrom":subQ0}),-1.0]])]});}
            extrude(context, id + "F4", {"entities" : qUnion([Q0]), "depth" : (getVariable(context, 'MaterialThickness')) * mm});
        }
        {
            var Q0;
            {var subQ0=sQuery(id+"F1.wireOp",EDGE,"E76.bottom");Q0=makeQuery(id+"F1.imprint","IMPRINT",FACE,{"disambiguationData":[TD([[makeQuery(id+"F1.imprint","IMPRINT",EDGE,{"derivedFrom":subQ0}),-1.0]])]});}
            var Q1;
            {var subQ3=sQuery(id+"F1.wireOp",EDGE,"E78.bottom");Q1=makeQuery(id+"F1.imprint","IMPRINT",FACE,{"disambiguationData":[TD([[makeQuery(id+"F1.imprint","IMPRINT",EDGE,{"derivedFrom":subQ3}),-1.0]])]});}
            var Q2;
            {var subQ0=sQuery(id+"F1.wireOp",EDGE,"E77.bottom");Q2=makeQuery(id+"F1.imprint","IMPRINT",FACE,{"disambiguationData":[TD([[makeQuery(id+"F1.imprint","IMPRINT",EDGE,{"derivedFrom":subQ0}),1.0]])]});}
            var Q3;
            Q3=makeQuery(id+"F1.imprint","IMPRINT",FACE,{"disambiguationData":[TD([[makeQuery(id+"F1.imprint","IMPRINT",EDGE,{"derivedFrom":sQuery(id+"F1.wireOp",EDGE,"E74.top")}),-1.0]])]});
            var Q4;
            Q4=makeQuery(id+"F1.imprint","IMPRINT",FACE,{"disambiguationData":[TD([[makeQuery(id+"F1.imprint","IMPRINT",EDGE,{"derivedFrom":sQuery(id+"F1.wireOp",EDGE,"E91.top")}),-1.0]])]});
            var Q5;
            Q5=makeQuery(id+"F1.imprint","IMPRINT",FACE,{"disambiguationData":[TD([[makeQuery(id+"F1.imprint","IMPRINT",EDGE,{"derivedFrom":sQuery(id+"F1.wireOp",EDGE,"E107.MirrorCS")}),1.0]])]});
            var Q6;
            {var subQ3=sQuery(id+"F1.wireOp",EDGE,"E113.MirrorCS");Q6=makeQuery(id+"F1.imprint","IMPRINT",FACE,{"disambiguationData":[TD([[makeQuery(id+"F1.imprint","IMPRINT",EDGE,{"derivedFrom":subQ3}),-1.0]])]});}
            var Q7;
            {var subQ0=sQuery(id+"F1.wireOp",EDGE,"E119.MirrorCS");Q7=makeQuery(id+"F1.imprint","IMPRINT",FACE,{"disambiguationData":[TD([[makeQuery(id+"F1.imprint","IMPRINT",EDGE,{"derivedFrom":subQ0}),1.0]])]});}
            var Q8;
            {var subQ0=sQuery(id+"F1.wireOp",EDGE,"E111.MirrorCS");Q8=makeQuery(id+"F1.imprint","IMPRINT",FACE,{"disambiguationData":[TD([[makeQuery(id+"F1.imprint","IMPRINT",EDGE,{"derivedFrom":subQ0}),-1.0]])]});}
            extrude(context, id + "F5", {"entities" : qUnion([Q0, Q1, Q2, Q3, Q4, Q5, Q6, Q7, Q8]), "depth" : (getVariable(context, 'MaterialThickness')) * mm});
        }
        {
            var Q0;
            {var subQ3=sQuery(id+"F1.wireOp",EDGE,"E4");var subQ5=sQuery(id+"F1.wireOp",EDGE,"E16.top");var subQ6=makeQuery(id+"F1.imprint","INTERSECT",VERTEX,{"derivedFrom":[subQ3,subQ5]});Q0=makeQuery(id+"F1.imprint","IMPRINT",FACE,{"disambiguationData":[TD([[makeQuery(id+"F1.imprint","IMPRINT",EDGE,{"disambiguationData":[TD([[subQ6,-1.0]])],"derivedFrom":subQ3}),-1.0]])]});}
            var Q1;
            {var subQ0=sQuery(id+"F1.wireOp",EDGE,"E6.left");var subQ3=sQuery(id+"F1.wireOp",EDGE,"E13.bottom");var subQ5=makeQuery(id+"F1.imprint","INTERSECT",VERTEX,{"derivedFrom":[subQ0,subQ3]});Q1=makeQuery(id+"F1.imprint","IMPRINT",FACE,{"disambiguationData":[TD([[makeQuery(id+"F1.imprint","IMPRINT",EDGE,{"disambiguationData":[TD([[subQ5,1.0]])],"derivedFrom":subQ3}),1.0]])]});}
            var Q2;
            {var subQ1=sQuery(id+"F1.wireOp",EDGE,"E3");var subQ3=sQuery(id+"F1.wireOp",EDGE,"E16.left");var subQ4=makeQuery(id+"F1.imprint","INTERSECT",VERTEX,{"derivedFrom":[subQ1,subQ3]});Q2=makeQuery(id+"F1.imprint","IMPRINT",FACE,{"disambiguationData":[TD([[makeQuery(id+"F1.imprint","IMPRINT",EDGE,{"disambiguationData":[TD([[subQ4,1.0]])],"derivedFrom":subQ3}),-1.0]])]});}
            var Q3;
            {var subQ0=sQuery(id+"F1.wireOp",EDGE,"E25.MirrorCS");var subQ3=sQuery(id+"F1.wireOp",EDGE,"E35.MirrorCS");var subQ5=makeQuery(id+"F1.imprint","INTERSECT",VERTEX,{"derivedFrom":[subQ0,subQ3]});Q3=makeQuery(id+"F1.imprint","IMPRINT",FACE,{"disambiguationData":[TD([[makeQuery(id+"F1.imprint","IMPRINT",EDGE,{"disambiguationData":[TD([[subQ5,1.0]])],"derivedFrom":subQ3}),1.0]])]});}
            var Q4;
            {var subQ0=sQuery(id+"F1.wireOp",EDGE,"E6.right");var subQ1=sQuery(id+"F1.wireOp",EDGE,"E6.top");var subQ2=makeQuery(id+"F1.imprint","INTERSECT",VERTEX,{"derivedFrom":[subQ1,subQ0]});Q4=makeQuery(id+"F1.imprint","IMPRINT",FACE,{"disambiguationData":[TD([[makeQuery(id+"F1.imprint","IMPRINT",EDGE,{"disambiguationData":[TD([[subQ2,1.0]])],"derivedFrom":subQ1}),1.0]])]});}
            var Q5;
            {var subQ0=sQuery(id+"F1.wireOp",EDGE,"E16.right");Q5=makeQuery(id+"F1.imprint","IMPRINT",FACE,{"disambiguationData":[TD([[makeQuery(id+"F1.imprint","IMPRINT",EDGE,{"derivedFrom":subQ0}),1.0]])]});}
            var Q6;
            {var subQ10=sQuery(id+"F1.wireOp",EDGE,"E5");Q6=makeQuery(id+"F1.imprint","IMPRINT",FACE,{"disambiguationData":[TD([[makeQuery(id+"F1.imprint","IMPRINT",EDGE,{"derivedFrom":subQ10}),-1.0]])]});}
            var Q7;
            {var subQ0=sQuery(id+"F1.wireOp",EDGE,"E9");Q7=makeQuery(id+"F1.imprint","IMPRINT",FACE,{"disambiguationData":[TD([[makeQuery(id+"F1.imprint","IMPRINT",EDGE,{"derivedFrom":subQ0}),1.0]])]});}
            var Q8;
            {var subQ0=sQuery(id+"F1.wireOp",EDGE,"E7");Q8=makeQuery(id+"F1.imprint","IMPRINT",FACE,{"disambiguationData":[TD([[makeQuery(id+"F1.imprint","IMPRINT",EDGE,{"derivedFrom":subQ0}),1.0]])]});}
            var Q9;
            {var subQ0=sQuery(id+"F1.wireOp",EDGE,"E10");Q9=makeQuery(id+"F1.imprint","IMPRINT",FACE,{"disambiguationData":[TD([[makeQuery(id+"F1.imprint","IMPRINT",EDGE,{"derivedFrom":subQ0}),1.0]])]});}
            var Q10;
            {var subQ1=sQuery(id+"F1.wireOp",EDGE,"E10");Q10=makeQuery(id+"F1.imprint","IMPRINT",FACE,{"disambiguationData":[TD([[makeQuery(id+"F1.imprint","IMPRINT",EDGE,{"derivedFrom":subQ1}),-1.0]])]});}
            var Q11;
            {var subQ0=sQuery(id+"F1.wireOp",EDGE,"E150");var subQ1=sQuery(id+"F1.wireOp",EDGE,"E19.MirrorCS");var subQ2=makeQuery(id+"F1.imprint","INTERSECT",VERTEX,{"disambiguationData":[OD(0.0)],"derivedFrom":[subQ1,subQ0]});Q11=makeQuery(id+"F1.imprint","IMPRINT",FACE,{"disambiguationData":[TD([[makeQuery(id+"F1.imprint","IMPRINT",EDGE,{"disambiguationData":[TD([[subQ2,-1.0]])],"derivedFrom":subQ1}),1.0]])]});}
            var Q12;
            {var subQ0=sQuery(id+"F1.wireOp",EDGE,"E151");var subQ1=sQuery(id+"F1.wireOp",EDGE,"E19.MirrorCS");var subQ5=makeQuery(id+"F1.imprint","INTERSECT",VERTEX,{"derivedFrom":[subQ1,subQ0]});Q12=makeQuery(id+"F1.imprint","IMPRINT",FACE,{"disambiguationData":[TD([[makeQuery(id+"F1.imprint","IMPRINT",EDGE,{"disambiguationData":[TD([[subQ5,1.0]])],"derivedFrom":subQ1}),1.0]])]});}
            var Q13;
            {var subQ0=sQuery(id+"F1.wireOp",EDGE,"E150");var subQ1=sQuery(id+"F1.wireOp",EDGE,"E19.MirrorCS");var subQ2=makeQuery(id+"F1.imprint","INTERSECT",VERTEX,{"disambiguationData":[OD(0.0)],"derivedFrom":[subQ1,subQ0]});Q13=makeQuery(id+"F1.imprint","IMPRINT",FACE,{"disambiguationData":[TD([[makeQuery(id+"F1.imprint","IMPRINT",EDGE,{"disambiguationData":[TD([[subQ2,-1.0]])],"derivedFrom":subQ1}),-1.0]])]});}
            var Q14;
            {var subQ1=sQuery(id+"F1.wireOp",EDGE,"E6.right");var subQ3=sQuery(id+"F1.wireOp",EDGE,"E30.MirrorCS");var subQ4=makeQuery(id+"F1.imprint","INTERSECT",VERTEX,{"derivedFrom":[subQ1,subQ3]});Q14=makeQuery(id+"F1.imprint","IMPRINT",FACE,{"disambiguationData":[TD([[makeQuery(id+"F1.imprint","IMPRINT",EDGE,{"disambiguationData":[TD([[subQ4,1.0]])],"derivedFrom":subQ3}),-1.0]])]});}
            extrude(context, id + "F6", {"entities" : qUnion([Q0, Q1, Q2, Q3, Q4, Q5, Q6, Q7, Q8, Q9, Q10, Q11, Q12, Q13, Q14]), "depth" : (getVariable(context, 'MaterialThickness')) * mm});
        }
        {
            var Q0;
            {var subQ0=sQuery(id+"F1.wireOp",EDGE,"E54.MirrorCS");Q0=makeQuery(id+"F1.imprint","IMPRINT",FACE,{"disambiguationData":[TD([[makeQuery(id+"F1.imprint","IMPRINT",EDGE,{"derivedFrom":subQ0}),1.0]])]});}
            var Q1;
            {var subQ4=sQuery(id+"F1.wireOp",EDGE,"E56.MirrorCS");Q1=makeQuery(id+"F1.imprint","IMPRINT",FACE,{"disambiguationData":[TD([[makeQuery(id+"F1.imprint","IMPRINT",EDGE,{"derivedFrom":subQ4}),-1.0]])]});}
            var Q2;
            {var subQ0=sQuery(id+"F1.wireOp",EDGE,"E49.MirrorCS");Q2=makeQuery(id+"F1.imprint","IMPRINT",FACE,{"disambiguationData":[TD([[makeQuery(id+"F1.imprint","IMPRINT",EDGE,{"derivedFrom":subQ0}),1.0]])]});}
            var Q3;
            {var subQ2=sQuery(id+"F1.wireOp",EDGE,"E43.right");Q3=makeQuery(id+"F1.imprint","IMPRINT",FACE,{"disambiguationData":[TD([[makeQuery(id+"F1.imprint","IMPRINT",EDGE,{"derivedFrom":subQ2}),-1.0]])]});}
            var Q4;
            Q4=makeQuery(id+"F1.imprint","IMPRINT",FACE,{"disambiguationData":[TD([[makeQuery(id+"F1.imprint","IMPRINT",EDGE,{"derivedFrom":sQuery(id+"F1.wireOp",EDGE,"E43.top")}),-1.0]])]});
            var Q5;
            {var subQ4=sQuery(id+"F1.wireOp",EDGE,"E41.bottom");Q5=makeQuery(id+"F1.imprint","IMPRINT",FACE,{"disambiguationData":[TD([[makeQuery(id+"F1.imprint","IMPRINT",EDGE,{"derivedFrom":subQ4}),1.0]])]});}
            var Q6;
            {var subQ0=sQuery(id+"F1.wireOp",EDGE,"E39.bottom");Q6=makeQuery(id+"F1.imprint","IMPRINT",FACE,{"disambiguationData":[TD([[makeQuery(id+"F1.imprint","IMPRINT",EDGE,{"derivedFrom":subQ0}),1.0]])]});}
            var Q7;
            {var subQ0=sQuery(id+"F1.wireOp",EDGE,"E40.bottom");Q7=makeQuery(id+"F1.imprint","IMPRINT",FACE,{"disambiguationData":[TD([[makeQuery(id+"F1.imprint","IMPRINT",EDGE,{"derivedFrom":subQ0}),-1.0]])]});}
            extrude(context, id + "F7", {"entities" : qUnion([Q0, Q1, Q2, Q3, Q4, Q5, Q6, Q7]), "depth" : (getVariable(context, 'MaterialThickness')) * mm});
        }
    });
